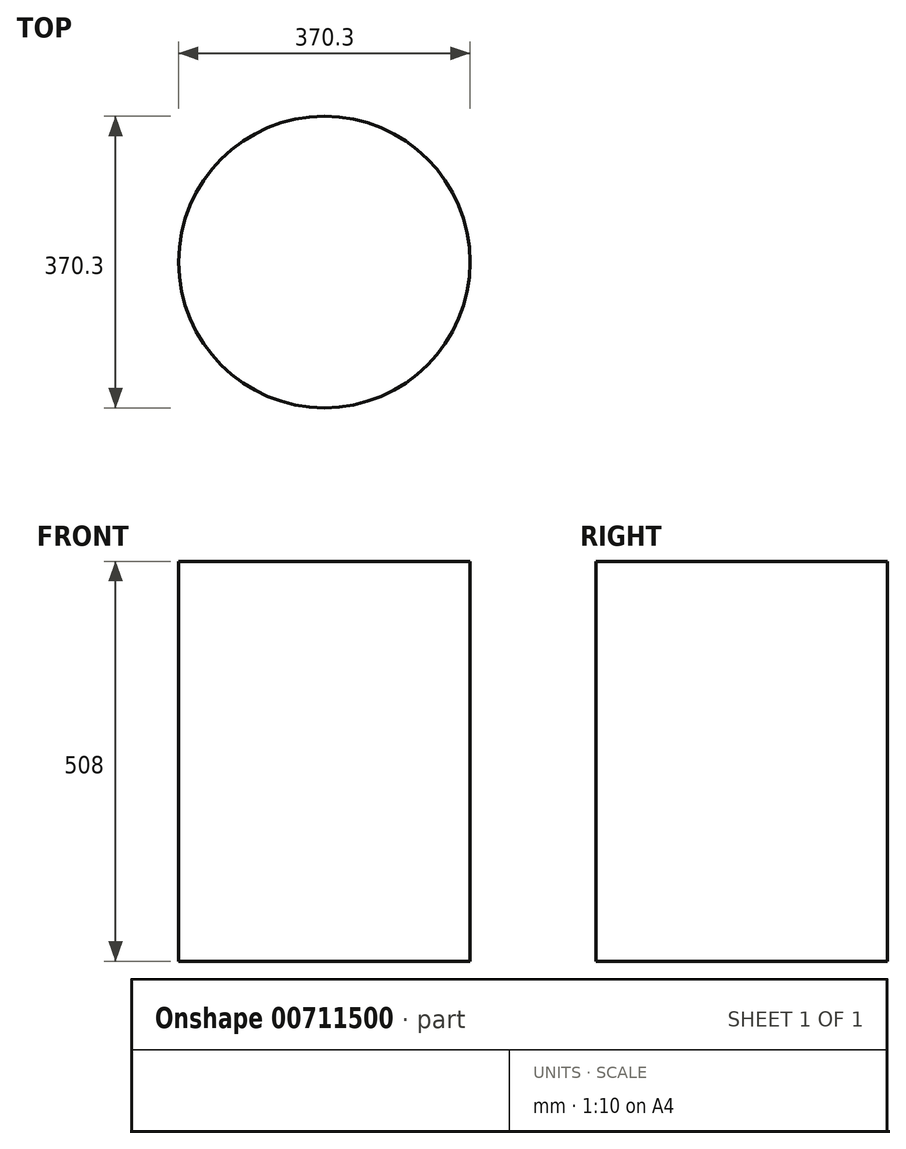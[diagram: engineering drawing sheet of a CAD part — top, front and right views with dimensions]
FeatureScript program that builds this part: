
annotation { "Feature Type Name" : "Feature", "Feature Type Description" : "" }
export const myFeature = defineFeature(function(context is Context, id is Id, definition is map)
    precondition{}
    {
        {
            var Q0;
            Q0=qCreatedBy(makeId("Top.planeOp"),FACE);
            var sketch = newSketch(context, id + "F0", { "sketchPlane" : qUnion([Q0])});
            skCircle(sketch, "E0", {"center": v(0, 0) * mm, "radius": 185.15 * mm});
            skSolve(sketch);
        }
        {
            var Q0;
            Q0=makeQuery(id+"F0.imprint","IMPRINT",FACE,{"disambiguationData":[TD([[makeQuery(id+"F0.imprint","IMPRINT",EDGE,{"derivedFrom":sQuery(id+"F0.wireOp",EDGE,"E0")}),1.0]])]});
            var Q1;
            Q1=sQuery(id+"F0.wireOp",EDGE,"E0");
            extrude(context, id + "F1", {"entities" : qUnion([Q0]), "bodyType" : ToolBodyType.SURFACE, "surfaceEntities" : qUnion([Q1]), "depth" : 508 * mm, "offsetDistance" : 25.4 * mm});
        }
    });
